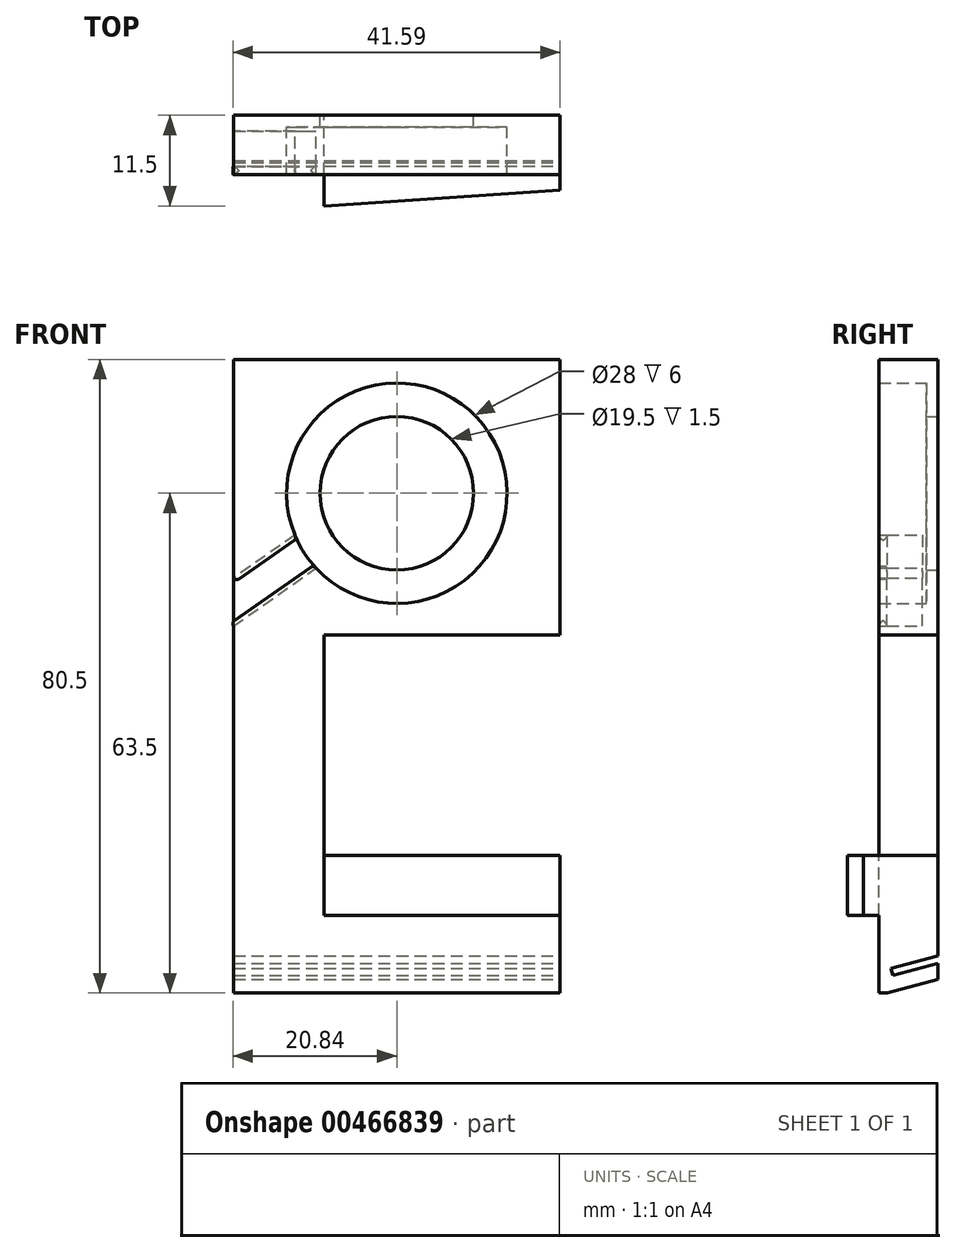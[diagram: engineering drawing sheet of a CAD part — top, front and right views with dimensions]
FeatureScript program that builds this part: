
annotation { "Feature Type Name" : "Feature", "Feature Type Description" : "" }
export const myFeature = defineFeature(function(context is Context, id is Id, definition is map)
    precondition{}
    {
        {
            var Q0;
            Q0=qCreatedBy(makeId("Front.planeOp"),FACE);
            var sketch = newSketch(context, id + "F0", { "sketchPlane" : qUnion([Q0])});
            skLineSegment(sketch, "E0.bottom", {"start": v(20.75, -40.25) * mm, "end": v(-20.75, -40.25) * mm});
            skLineSegment(sketch, "E0.top", {"start": v(20.75, 40.25) * mm, "end": v(-20.75, 40.25) * mm});
            skLineSegment(sketch, "E0.left", {"start": v(20.75, -40.25) * mm, "end": v(20.75, 40.25) * mm});
            skLineSegment(sketch, "E0.right", {"start": v(-20.75, -40.25) * mm, "end": v(-20.75, 40.25) * mm});
            skPoint(sketch, "E0.middle", {"position": v(0, 0) * mm});
            skCircle(sketch, "E1", {"center": v(0, 23.25) * mm, "radius": 14 * mm});
            skLineSegment(sketch, "E2.bottom", {"start": v(-9.25, 5.25) * mm, "end": v(20.75, 5.25) * mm});
            skLineSegment(sketch, "E2.top", {"start": v(-9.25, -22.75) * mm, "end": v(20.75, -22.75) * mm});
            skLineSegment(sketch, "E2.left", {"start": v(-9.25, 5.25) * mm, "end": v(-9.25, -22.75) * mm});
            skLineSegment(sketch, "E2.right", {"start": v(20.75, 5.25) * mm, "end": v(20.75, -22.75) * mm});
            skCircle(sketch, "E3", {"center": v(0, 23.25) * mm, "radius": 9.75 * mm});
            skLineSegment(sketch, "E4", {"start": v(0, 23.25) * mm, "end": v(-21.85, 7.95) * mm, "construction": true});
            skLineSegment(sketch, "E5", {"start": v(-20.75, 6.37) * mm, "end": v(0, 20.9) * mm});
            skLineSegment(sketch, "E6", {"start": v(0, 27) * mm, "end": v(-20.75, 12.48) * mm});
            skLineSegment(sketch, "E7", {"start": v(0, 23.25) * mm, "end": v(-20.75, 23.25) * mm, "construction": true});
            skSolve(sketch);
        }
        {
            var Q0;
            {var subQ4=sQuery(id+"F0.wireOp",EDGE,"E0.bottom");Q0=makeQuery(id+"F0.imprint","IMPRINT",FACE,{"disambiguationData":[TD([[makeQuery(id+"F0.imprint","IMPRINT",EDGE,{"derivedFrom":subQ4}),-1.0]])]});}
            extrude(context, id + "F1", {"entities" : qUnion([Q0]), "depth" : 7.5 * mm});
        }
        {
            var Q0;
            Q0=makeQuery(id+"F0.imprint","IMPRINT",FACE,{"disambiguationData":[TD([[makeQuery(id+"F0.imprint","IMPRINT",EDGE,{"derivedFrom":sQuery(id+"F0.wireOp",EDGE,"E1")}),1.0]])]});
            extrude(context, id + "F2", {"entities" : qUnion([Q0]), "operationType" : NewBodyOperationType.ADD, "depth" : 1.5 * mm});
        }
        {
            var Q0;
            {var subQ0=sQuery(id+"F0.wireOp",EDGE,"E5");var subQ1=sQuery(id+"F0.wireOp",EDGE,"E0.right");var subQ2=makeQuery(id+"F0.imprint","INTERSECT",VERTEX,{"derivedFrom":[subQ1,subQ0]});Q0=makeQuery(id+"F0.imprint","IMPRINT",FACE,{"disambiguationData":[TD([[makeQuery(id+"F0.imprint","IMPRINT",EDGE,{"disambiguationData":[TD([[subQ2,-1.0]])],"derivedFrom":subQ1}),-1.0]])]});}
            extrude(context, id + "F3", {"entities" : qUnion([Q0]), "operationType" : NewBodyOperationType.ADD, "depth" : 2 * mm});
        }
        {
            var Q0;
            {var subQ0=sQuery(id+"F0.wireOp",EDGE,"E0.left");Q0=makeQuery(id+"F1.opExtrude","SWEPT_FACE",FACE,{"disambiguationData":[OSD([subQ0]),TDD([makeQuery(id+"F0.imprint","IMPRINT",EDGE,{"disambiguationData":[TD([[makeQuery(id+"F0.imprint","INTERSECT",VERTEX,{"derivedFrom":[sQuery(id+"F0.wireOp",EDGE,"E0.bottom"),subQ0]}),-1.0]])],"derivedFrom":subQ0})])]});}
            var sketch = newSketch(context, id + "F4", { "sketchPlane" : qUnion([Q0])});
            skLineSegment(sketch, "E8", {"start": v(0, -40.25) * mm, "end": v(0, -38.53) * mm});
            skLineSegment(sketch, "E9", {"start": v(0, -38.53) * mm, "end": v(-6.44, -40.25) * mm});
            skLineSegment(sketch, "E10", {"start": v(-6.44, -40.25) * mm, "end": v(0, -40.25) * mm});
            skLineSegment(sketch, "E11", {"start": v(0, -36.45) * mm, "end": v(-5.77, -38) * mm});
            skLineSegment(sketch, "E12", {"start": v(-5.77, -38) * mm, "end": v(-6, -37.13) * mm});
            skLineSegment(sketch, "E13", {"start": v(-6, -37.13) * mm, "end": v(0, -35.52) * mm});
            skLineSegment(sketch, "E14", {"start": v(0, -35.52) * mm, "end": v(0, -36.45) * mm});
            skSolve(sketch);
        }
        {
            var Q0;
            Q0=makeQuery(id+"F4.imprint","IMPRINT",FACE,{"disambiguationData":[TD([[makeQuery(id+"F4.imprint","IMPRINT",EDGE,{"derivedFrom":sQuery(id+"F4.wireOp",EDGE,"E8")}),1.0]])]});
            extrude(context, id + "F5", {"entities" : qUnion([Q0]), "operationType" : NewBodyOperationType.REMOVE, "oppositeDirection" : true, "depth" : 45 * mm});
        }
        {
            var Q0;
            Q0=makeQuery(id+"F4.imprint","IMPRINT",FACE,{"disambiguationData":[TD([[makeQuery(id+"F4.imprint","IMPRINT",EDGE,{"derivedFrom":sQuery(id+"F4.wireOp",EDGE,"E11")}),-1.0]])]});
            extrude(context, id + "F6", {"entities" : qUnion([Q0]), "operationType" : NewBodyOperationType.REMOVE, "oppositeDirection" : true, "depth" : 45 * mm});
        }
        {
            var Q0;
            Q0=makeQuery(id+"F1.opExtrude","SWEPT_FACE",FACE,{"disambiguationData":[OSD([sQuery(id+"F0.wireOp",EDGE,"E6")])]});
            var sketch = newSketch(context, id + "F7", { "sketchPlane" : qUnion([Q0])});
            skLineSegment(sketch, "E15", {"start": v(-9.84, 7.5) * mm, "end": v(-0.32, 7.5) * mm});
            skLineSegment(sketch, "E16", {"start": v(-0.32, 7.5) * mm, "end": v(-0.32, 6.5) * mm});
            skLineSegment(sketch, "E17", {"start": v(-0.32, 6.5) * mm, "end": v(-9.84, 6.5) * mm});
            skLineSegment(sketch, "E18", {"start": v(-9.84, 6.5) * mm, "end": v(-9.84, 7.5) * mm});
            skSolve(sketch);
        }
        {
            var Q0;
            Q0=makeQuery(id+"F7.imprint","IMPRINT",FACE,{"disambiguationData":[TD([[makeQuery(id+"F7.imprint","IMPRINT",EDGE,{"derivedFrom":sQuery(id+"F7.wireOp",EDGE,"E15")}),1.0]])]});
            extrude(context, id + "F8", {"entities" : qUnion([Q0]), "operationType" : NewBodyOperationType.ADD, "depth" : 0.5 * mm});
        }
        {
            var Q0;
            Q0=makeQuery(id+"F1.opExtrude","SWEPT_FACE",FACE,{"disambiguationData":[OSD([sQuery(id+"F0.wireOp",EDGE,"E5")])]});
            var sketch = newSketch(context, id + "F9", { "sketchPlane" : qUnion([Q0])});
            skLineSegment(sketch, "E19", {"start": v(-0.53, -7.5) * mm, "end": v(-13.34, -7.5) * mm});
            skLineSegment(sketch, "E20", {"start": v(-13.34, -7.5) * mm, "end": v(-13.34, -6.5) * mm});
            skLineSegment(sketch, "E21", {"start": v(-13.34, -6.5) * mm, "end": v(-0.53, -6.5) * mm});
            skLineSegment(sketch, "E22", {"start": v(-0.53, -6.5) * mm, "end": v(-0.53, -7.5) * mm});
            skSolve(sketch);
        }
        {
            var Q0;
            Q0=makeQuery(id+"F9.imprint","IMPRINT",FACE,{"disambiguationData":[TD([[makeQuery(id+"F9.imprint","IMPRINT",EDGE,{"derivedFrom":sQuery(id+"F9.wireOp",EDGE,"E19")}),1.0]])]});
            extrude(context, id + "F10", {"entities" : qUnion([Q0]), "operationType" : NewBodyOperationType.ADD, "depth" : 0.5 * mm});
        }
        {
            var Q0;
            Q0=makeQuery(id+"F8.opExtrude","CAP_FACE",FACE,{"disambiguationData":[OSD([sQuery(id+"F7.wireOp",EDGE,"E15"),sQuery(id+"F7.wireOp",EDGE,"E16"),sQuery(id+"F7.wireOp",EDGE,"E17"),sQuery(id+"F7.wireOp",EDGE,"E18")])],"isStart":false});
            fillet(context, id + "F11", {"entities" : qUnion([Q0]), "radius" : 0.5 * mm, "tangentPropagation" : true, "allowEdgeOverflow" : false});
        }
        {
            var Q0;
            Q0=makeQuery(id+"F10.opExtrude","CAP_FACE",FACE,{"disambiguationData":[OSD([sQuery(id+"F9.wireOp",EDGE,"E19"),sQuery(id+"F9.wireOp",EDGE,"E20"),sQuery(id+"F9.wireOp",EDGE,"E21"),sQuery(id+"F9.wireOp",EDGE,"E22")])],"isStart":false});
            fillet(context, id + "F12", {"entities" : qUnion([Q0]), "radius" : 0.5 * mm, "tangentPropagation" : true, "allowEdgeOverflow" : false});
        }
        {
            var Q0;
            {var subQ0=sQuery(id+"F0.wireOp",EDGE,"E0.right");var subQ1=sQuery(id+"F0.wireOp",EDGE,"E0.left");var subQ2=sQuery(id+"F0.wireOp",EDGE,"E0.bottom");var subQ4=sQuery(id+"F0.wireOp",EDGE,"E2.top");var subQ5=sQuery(id+"F0.wireOp",EDGE,"E2.left");var subQ6=sQuery(id+"F0.wireOp",EDGE,"E2.bottom");var subQ7=sQuery(id+"F0.wireOp",EDGE,"E3");var subQ8=sQuery(id+"F0.wireOp",EDGE,"E0.top");var subQ9=sQuery(id+"F0.wireOp",EDGE,"E6");var subQ10=sQuery(id+"F0.wireOp",EDGE,"E5");var subQ11=sQuery(id+"F0.wireOp",EDGE,"E1");Q0=makeQuery(id+"F6.boolean.opBoolean","SPLIT",FACE,{"disambiguationData":[TD([makeQuery(id+"F1.opExtrude","SWEPT_FACE",FACE,{"disambiguationData":[OSD([subQ8])]})])],"derivedFrom":makeQuery(id+"F3.boolean.opBoolean","MERGE",FACE,{"derivedFrom":[makeQuery(id+"F2.boolean.opBoolean","MERGE",FACE,{"derivedFrom":[makeQuery(id+"F1.opExtrude","CAP_FACE",FACE,{"disambiguationData":[OSD([subQ2,subQ8,subQ1,subQ0,subQ11,subQ6,subQ4,subQ5,subQ10,subQ9])],"isStart":true}),makeQuery(id+"F2.opExtrude","CAP_FACE",FACE,{"disambiguationData":[OSD([subQ11,subQ7])],"isStart":true})]}),makeQuery(id+"F3.opExtrude","CAP_FACE",FACE,{"disambiguationData":[OSD([subQ0,subQ11,subQ10,subQ9])],"isStart":true})]})});}
            var sketch = newSketch(context, id + "F13", { "sketchPlane" : qUnion([Q0])});
            skLineSegment(sketch, "E23", {"start": v(9.25, -22.75) * mm, "end": v(9.25, -30.39) * mm});
            skLineSegment(sketch, "E24", {"start": v(9.25, -30.39) * mm, "end": v(-20.75, -30.39) * mm});
            skLineSegment(sketch, "E25", {"start": v(-20.75, -30.39) * mm, "end": v(-20.75, -22.75) * mm});
            skLineSegment(sketch, "E26", {"start": v(-20.75, -22.75) * mm, "end": v(9.25, -22.75) * mm});
            skSolve(sketch);
        }
        {
            var Q0;
            Q0=makeQuery(id+"F13.imprint","IMPRINT",FACE,{"disambiguationData":[TD([[makeQuery(id+"F13.imprint","IMPRINT",EDGE,{"derivedFrom":sQuery(id+"F13.wireOp",EDGE,"E23")}),-1.0]])]});
            extrude(context, id + "F14", {"entities" : qUnion([Q0]), "operationType" : NewBodyOperationType.ADD, "oppositeDirection" : true, "depth" : 11.5 * mm});
        }
        {
            var Q0;
            Q0=makeQuery(id+"F14.opExtrude","SWEPT_FACE",FACE,{"disambiguationData":[OSD([sQuery(id+"F13.wireOp",EDGE,"E24")])]});
            var sketch = newSketch(context, id + "F15", { "sketchPlane" : qUnion([Q0])});
            skLineSegment(sketch, "E27", {"start": v(20.75, 9.5) * mm, "end": v(-9.25, 11.5) * mm});
            skLineSegment(sketch, "E28", {"start": v(-9.25, 11.5) * mm, "end": v(20.75, 11.5) * mm});
            skLineSegment(sketch, "E29", {"start": v(20.75, 9.5) * mm, "end": v(20.75, 11.5) * mm});
            skSolve(sketch);
        }
        {
            var Q0;
            Q0=makeQuery(id+"F15.imprint","IMPRINT",FACE,{"disambiguationData":[TD([[makeQuery(id+"F15.imprint","IMPRINT",EDGE,{"derivedFrom":sQuery(id+"F15.wireOp",EDGE,"E27")}),-1.0]])]});
            extrude(context, id + "F16", {"entities" : qUnion([Q0]), "operationType" : NewBodyOperationType.REMOVE, "endBound" : BoundingType.SYMMETRIC, "depth" : 25 * mm});
        }
    });
